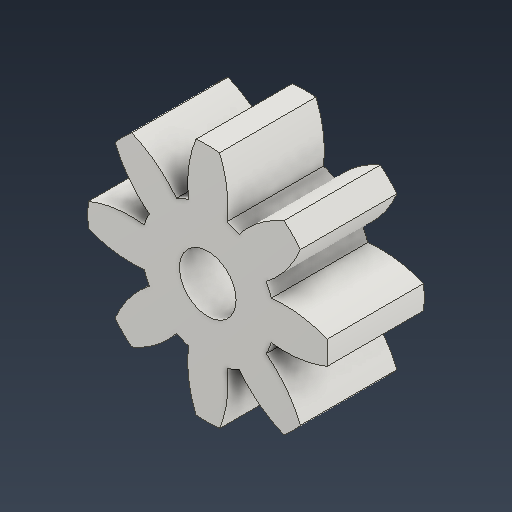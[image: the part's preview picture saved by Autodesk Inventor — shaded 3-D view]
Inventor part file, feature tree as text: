
AUTODESK INVENTOR PART (.ipt)
format: ipt  version: 2025.3 (Build 293356000, 356)  size: 199,680 bytes
history: native  units: mm (DEFAULTED — no unit token found)
features: plane x3, other x3, extrude x2, sketch x2
ambient origin geometry x8: Origin, YZ Plane, XZ Plane, XY Plane, X Axis, Y Axis, Z Axis, Center Point
bodies: Solid1 (feature_tree)
feature tree (10):
  extrude  "Extrusion1"  Depth=4.0mm TaperAngle=0.0deg
  plane  "Work Plane2"
  plane  "Work Plane8"
  plane  "Work Plane9"
  other  "正齒輪"
  extrude  "擠出2"  Depth=10.0mm
  sketch  "Sketch1"  dims[d0=9.95296mm d1=4.0mm d2=0.0mm d3=8.0mm d4=10.0mm d5=0.0mm d16=23.624533mm d17=0.0mm d34=22.5deg d39=0.0mm d41=0.0mm d43=23.624533mm d46=23.624533mm d47=0.0mm d48=0.0mm d49=2.35mm d50=10.0mm d51=0.0mm]
  other  "Srf1"
  sketch  "草圖3"
  other  "節圓直徑"
